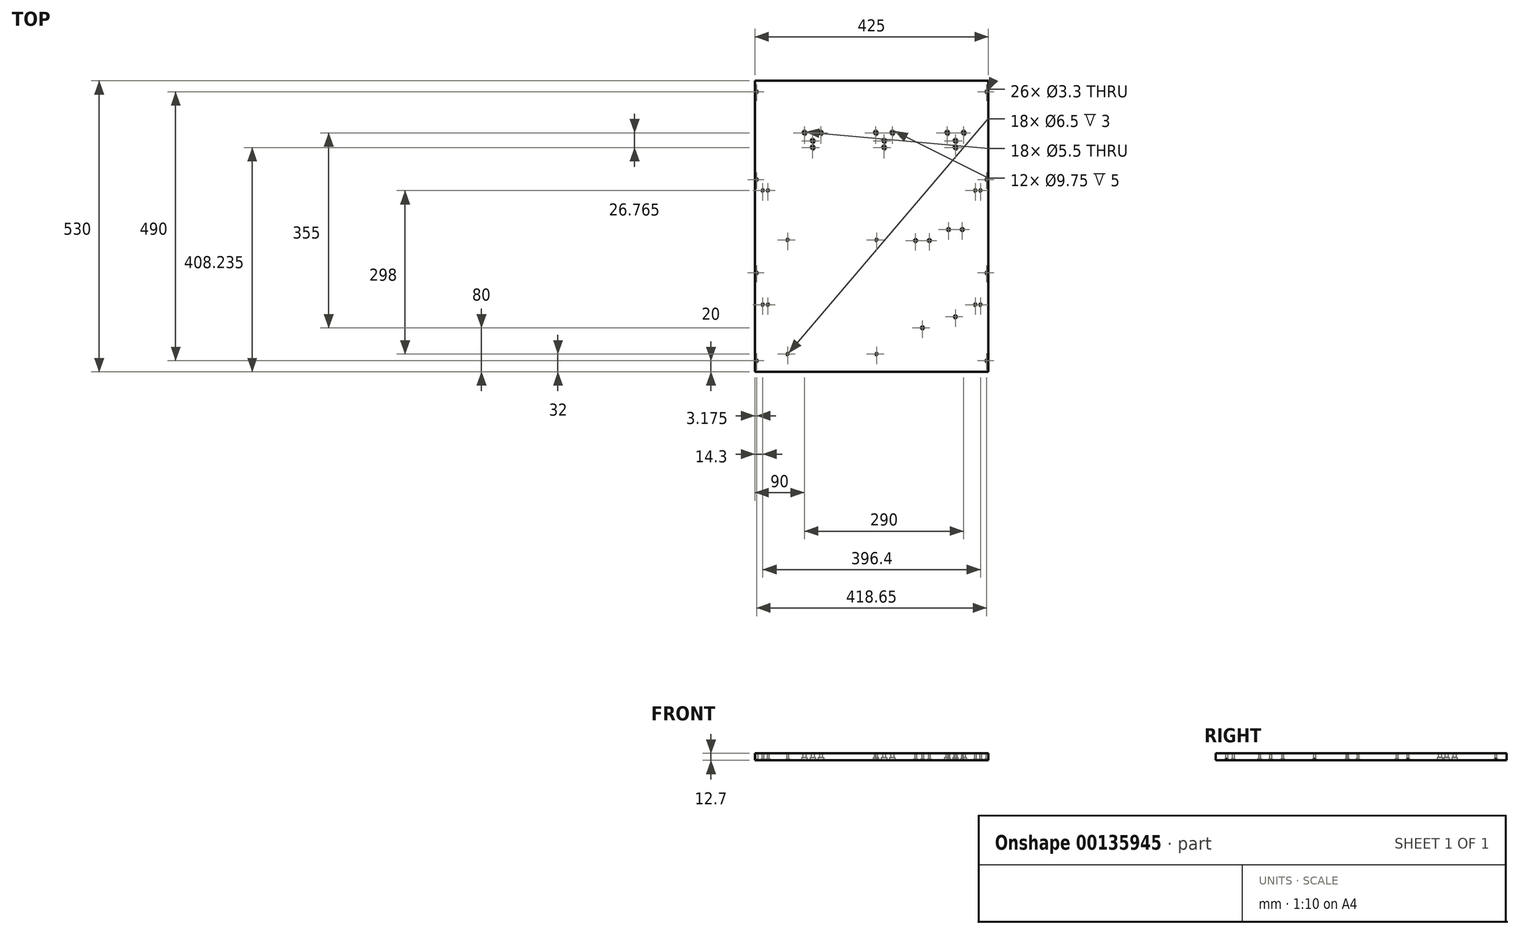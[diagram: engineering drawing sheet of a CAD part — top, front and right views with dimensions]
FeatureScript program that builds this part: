
annotation { "Feature Type Name" : "Feature", "Feature Type Description" : "" }
export const myFeature = defineFeature(function(context is Context, id is Id, definition is map)
    precondition{}
    {
        {
            var Q0;
            Q0=qCreatedBy(makeId("Top.planeOp"),FACE);
            var sketch = newSketch(context, id + "F0", { "sketchPlane" : qUnion([Q0])});
            skLineSegment(sketch, "E0.bottom", {"start": v(212.5, -265) * mm, "end": v(-212.5, -265) * mm});
            skLineSegment(sketch, "E0.top", {"start": v(212.5, 265) * mm, "end": v(-212.5, 265) * mm});
            skLineSegment(sketch, "E0.left", {"start": v(212.5, -265) * mm, "end": v(212.5, 265) * mm});
            skLineSegment(sketch, "E0.right", {"start": v(-212.5, -265) * mm, "end": v(-212.5, 265) * mm});
            skPoint(sketch, "E0.middle", {"position": v(0, 0) * mm});
            skLineSegment(sketch, "E1.top", {"start": v(81.24, -196.03) * mm, "end": v(129.3, -196.03) * mm});
            skSolve(sketch);
        }
        {
            var Q0;
            Q0 = qSketchRegion(id + "F0", true);
            extrude(context, id + "F1", {"entities" : qUnion([Q0]), "endBound" : BoundingType.SYMMETRIC, "depth" : 12.7 * mm});
        }
        {
            var Q0;
            Q0=makeQuery(id+"F1.opExtrude","CAP_FACE",FACE,{"disambiguationData":[OSD([sQuery(id+"F0.wireOp",EDGE,"E0.bottom"),sQuery(id+"F0.wireOp",EDGE,"E0.top"),sQuery(id+"F0.wireOp",EDGE,"E0.left"),sQuery(id+"F0.wireOp",EDGE,"E0.right")])],"isStart":true});
            var sketch = newSketch(context, id + "F2", { "sketchPlane" : qUnion([Q0])});
            skCircle(sketch, "E2", {"center": v(-209.33, 245) * mm, "radius": 2 * mm});
            skCircle(sketch, "E3", {"center": v(-209.33, 85) * mm, "radius": 2 * mm});
            skCircle(sketch, "E4.MirrorC", {"center": v(-209.33, -85) * mm, "radius": 2 * mm});
            skCircle(sketch, "E5.MirrorC", {"center": v(-209.33, -245) * mm, "radius": 2 * mm});
            skCircle(sketch, "E6.MirrorC", {"center": v(209.33, 245) * mm, "radius": 2 * mm});
            skCircle(sketch, "E7.MirrorC", {"center": v(209.33, 85) * mm, "radius": 2 * mm});
            skCircle(sketch, "E8.MirrorC", {"center": v(209.33, -85) * mm, "radius": 2 * mm});
            skCircle(sketch, "E9.MirrorC", {"center": v(209.33, -245) * mm, "radius": 2 * mm});
            skCircle(sketch, "E10", {"center": v(-198.2, 143) * mm, "radius": 2 * mm});
            skLineSegment(sketch, "E11", {"start": v(0, 0) * mm, "end": v(0, 264.7) * mm});
            skCircle(sketch, "E12", {"center": v(-188.7, 143) * mm, "radius": 2 * mm});
            skCircle(sketch, "E13.MirrorC", {"center": v(198.2, 143) * mm, "radius": 2 * mm});
            skCircle(sketch, "E14.MirrorC", {"center": v(188.7, 143) * mm, "radius": 2 * mm});
            skCircle(sketch, "E15", {"center": v(-198.2, -65) * mm, "radius": 2 * mm});
            skCircle(sketch, "E16", {"center": v(-188.7, -65) * mm, "radius": 2 * mm});
            skCircle(sketch, "E17.MirrorC", {"center": v(188.7, -65) * mm, "radius": 2 * mm});
            skCircle(sketch, "E18.MirrorC", {"center": v(198.2, -65) * mm, "radius": 2 * mm});
            skSolve(sketch);
        }
        {
            var Q0;
            Q0=sQuery(id+"F2.wireOp",VERTEX,"E2.center");
            var Q1;
            Q1=sQuery(id+"F2.wireOp",VERTEX,"E3.center");
            var Q2;
            Q2=sQuery(id+"F2.wireOp",VERTEX,"E4.MirrorC.center");
            var Q3;
            Q3=sQuery(id+"F2.wireOp",VERTEX,"E5.MirrorC.center");
            var Q4;
            Q4=sQuery(id+"F2.wireOp",VERTEX,"E9.MirrorC.center");
            var Q5;
            Q5=sQuery(id+"F2.wireOp",VERTEX,"E8.MirrorC.center");
            var Q6;
            Q6=sQuery(id+"F2.wireOp",VERTEX,"E7.MirrorC.center");
            var Q7;
            Q7=sQuery(id+"F2.wireOp",VERTEX,"E6.MirrorC.center");
            var Q8;
            Q8=sQuery(id+"F2.wireOp",VERTEX,"E10.center");
            var Q9;
            Q9=sQuery(id+"F2.wireOp",VERTEX,"WoDvKdXF-PdJz-WFzz-Z4uX-elENKUMFdGKx.center");
            var Q10;
            Q10=sQuery(id+"F2.wireOp",VERTEX,"axoy2mSQ-Yy3T-ROeZ-40XW-cdWlI4RzoubP.center");
            var Q11;
            Q11=sQuery(id+"F2.wireOp",VERTEX,"Gf7lKQ4c-8bLx-3h7W-wmy7-qyMdfDCTACcy.center");
            var Q12;
            Q12=sQuery(id+"F2.wireOp",VERTEX,"afeb9733-eb6e-4099-b4cc-138f5442d24a0.MirrorC.center");
            var Q13;
            Q13=sQuery(id+"F2.wireOp",VERTEX,"5a1a8710-edd7-43ff-9459-da1546c242ab0.MirrorC.center");
            var Q14;
            Q14=sQuery(id+"F2.wireOp",VERTEX,"c1e0f906-5fed-4c0f-b8fc-75f51ee2fa860.MirrorC.center");
            var Q15;
            Q15=sQuery(id+"F2.wireOp",VERTEX,"86eb54a1-4769-462b-b598-50202e1166000.MirrorC.center");
            var Q16;
            Q16=sQuery(id+"F2.wireOp",VERTEX,"6J1cC2zl-gnNa-lyWi-kusl-kWZGhb2Tm6Yi.center");
            var Q17;
            Q17=sQuery(id+"F2.wireOp",VERTEX,"2Pyidt3F-xQNL-qOz5-DrPg-jibaZAFIGgOY.center");
            var Q18;
            Q18=sQuery(id+"F2.wireOp",VERTEX,"3b745f28-dec8-4eaf-b7a0-753a52fb6e040.MirrorC.center");
            var Q19;
            Q19=sQuery(id+"F2.wireOp",VERTEX,"65bc9fd0-061f-4973-9c23-7b2eaf92318f0.MirrorC.center");
            var Q20;
            Q20=sQuery(id+"F2.wireOp",VERTEX,"E12.center");
            var Q21;
            Q21=sQuery(id+"F2.wireOp",VERTEX,"E13.MirrorC.center");
            var Q22;
            Q22=sQuery(id+"F2.wireOp",VERTEX,"E14.MirrorC.center");
            var Q23;
            Q23=sQuery(id+"F2.wireOp",VERTEX,"E15.center");
            var Q24;
            Q24=sQuery(id+"F2.wireOp",VERTEX,"E16.center");
            var Q25;
            Q25=sQuery(id+"F2.wireOp",VERTEX,"E17.MirrorC.center");
            var Q26;
            Q26=sQuery(id+"F2.wireOp",VERTEX,"E18.MirrorC.center");
            var Q27;
            Q27=makeQuery(id+"F1.opExtrude","SWEPT_BODY",BODY,{"disambiguationData":[OSD([sQuery(id+"F0.wireOp",EDGE,"E0.bottom"),sQuery(id+"F0.wireOp",EDGE,"E0.top"),sQuery(id+"F0.wireOp",EDGE,"E0.left"),sQuery(id+"F0.wireOp",EDGE,"E0.right")])]});
            hole(context, id + "F3", {"style" : HoleStyle.C_BORE, "endStyle" : HoleEndStyle.THROUGH, "standardTappedOrClearance" : lookupTablePath({ "standard" : "ISO", "fit" : "Normal", "size" : "M3", "type" : "Clearance" }), "standardBlindInLast" : lookupTablePath({ "fit" : "Standard", "standard" : "ISO", "size" : "M3", "type" : "Clearance" }), "holeDiameter" : 3.3 * mm, "cBoreDiameter" : 6.5 * mm, "cBoreDepth" : 3 * mm, "locations" : qUnion([Q0, Q1, Q2, Q3, Q4, Q5, Q6, Q7, Q8, Q9, Q10, Q11, Q12, Q13, Q14, Q15, Q16, Q17, Q18, Q19, Q20, Q21, Q22, Q23, Q24, Q25, Q26]), "scope" : qUnion([Q27]), "isTappedThrough" : true});
        }
        {
            var Q0;
            Q0=makeQuery(id+"F1.opExtrude","CAP_FACE",FACE,{"disambiguationData":[OSD([sQuery(id+"F0.wireOp",EDGE,"E0.bottom"),sQuery(id+"F0.wireOp",EDGE,"E0.top"),sQuery(id+"F0.wireOp",EDGE,"E0.left"),sQuery(id+"F0.wireOp",EDGE,"E0.right")])],"isStart":true});
            var sketch = newSketch(context, id + "F4", { "sketchPlane" : qUnion([Q0])});
            skCircle(sketch, "E19", {"center": v(-122.5, -170) * mm, "radius": 2 * mm});
            skCircle(sketch, "E20", {"center": v(-92.5, -170) * mm, "radius": 2 * mm});
            skCircle(sketch, "E21", {"center": v(-107.5, -155.23) * mm, "radius": 2 * mm});
            skCircle(sketch, "E22", {"center": v(-107.5, -143.23) * mm, "radius": 2 * mm});
            skCircle(sketch, "E23", {"center": v(137.5, -170) * mm, "radius": 2 * mm});
            skCircle(sketch, "E24", {"center": v(167.5, -170) * mm, "radius": 2 * mm});
            skCircle(sketch, "E25", {"center": v(152.5, -155.24) * mm, "radius": 2 * mm});
            skCircle(sketch, "E26", {"center": v(152.5, -143.24) * mm, "radius": 2 * mm});
            skCircle(sketch, "E27", {"center": v(7.5, -170) * mm, "radius": 2 * mm});
            skCircle(sketch, "E28", {"center": v(37.5, -170) * mm, "radius": 2 * mm});
            skCircle(sketch, "E29", {"center": v(22.5, -155.23) * mm, "radius": 2 * mm});
            skCircle(sketch, "E30", {"center": v(22.5, -143.23) * mm, "radius": 2 * mm});
            skSolve(sketch);
        }
        {
            var Q0;
            Q0=sQuery(id+"F4.wireOp",VERTEX,"E19.center");
            var Q1;
            Q1=sQuery(id+"F4.wireOp",VERTEX,"E20.center");
            var Q2;
            Q2=sQuery(id+"F4.wireOp",VERTEX,"E21.center");
            var Q3;
            Q3=sQuery(id+"F4.wireOp",VERTEX,"E22.center");
            var Q4;
            Q4=sQuery(id+"F4.wireOp",VERTEX,"E24.center");
            var Q5;
            Q5=sQuery(id+"F4.wireOp",VERTEX,"E25.center");
            var Q6;
            Q6=sQuery(id+"F4.wireOp",VERTEX,"E26.center");
            var Q7;
            Q7=sQuery(id+"F4.wireOp",VERTEX,"E23.center");
            var Q8;
            Q8=sQuery(id+"F4.wireOp",VERTEX,"E28.center");
            var Q9;
            Q9=sQuery(id+"F4.wireOp",VERTEX,"E27.center");
            var Q10;
            Q10=sQuery(id+"F4.wireOp",VERTEX,"E29.center");
            var Q11;
            Q11=sQuery(id+"F4.wireOp",VERTEX,"E30.center");
            var Q12;
            Q12=makeQuery(id+"F1.opExtrude","SWEPT_BODY",BODY,{"disambiguationData":[OSD([sQuery(id+"F0.wireOp",EDGE,"E0.bottom"),sQuery(id+"F0.wireOp",EDGE,"E0.top"),sQuery(id+"F0.wireOp",EDGE,"E0.left"),sQuery(id+"F0.wireOp",EDGE,"E0.right")])]});
            hole(context, id + "F5", {"style" : HoleStyle.C_BORE, "endStyle" : HoleEndStyle.THROUGH, "standardTappedOrClearance" : lookupTablePath({ "standard" : "ISO", "fit" : "Normal", "size" : "M5", "type" : "Clearance" }), "standardBlindInLast" : lookupTablePath({ "fit" : "Standard", "standard" : "ISO", "size" : "M5", "type" : "Clearance" }), "holeDiameter" : 5.5 * mm, "cBoreDiameter" : 9.75 * mm, "cBoreDepth" : 5 * mm, "locations" : qUnion([Q0, Q1, Q2, Q3, Q4, Q5, Q6, Q7, Q8, Q9, Q10, Q11]), "scope" : qUnion([Q12]), "isTappedThrough" : true});
        }
        {
            var Q0;
            Q0=makeQuery(id+"F1.opExtrude","CAP_FACE",FACE,{"disambiguationData":[OSD([sQuery(id+"F0.wireOp",EDGE,"E0.bottom"),sQuery(id+"F0.wireOp",EDGE,"E0.top"),sQuery(id+"F0.wireOp",EDGE,"E0.left"),sQuery(id+"F0.wireOp",EDGE,"E0.right")])],"isStart":true});
            var sketch = newSketch(context, id + "F6", { "sketchPlane" : qUnion([Q0])});
            skCircle(sketch, "E31", {"center": v(152.5, 165) * mm, "radius": 1.5 * mm});
            skCircle(sketch, "E32", {"center": v(165, 6) * mm, "radius": 1.5 * mm});
            skCircle(sketch, "E33", {"center": v(140, 6) * mm, "radius": 1.5 * mm});
            skCircle(sketch, "E34", {"center": v(92.5, 185) * mm, "radius": 1.5 * mm});
            skCircle(sketch, "E35", {"center": v(105, 26) * mm, "radius": 1.5 * mm});
            skCircle(sketch, "E36", {"center": v(80, 26) * mm, "radius": 1.5 * mm});
            skSolve(sketch);
        }
        {
            var Q0;
            Q0=sQuery(id+"F6.wireOp",VERTEX,"E31.center");
            var Q1;
            Q1=sQuery(id+"F6.wireOp",VERTEX,"E32.center");
            var Q2;
            Q2=sQuery(id+"F6.wireOp",VERTEX,"E33.center");
            var Q3;
            Q3=sQuery(id+"F6.wireOp",VERTEX,"E34.center");
            var Q4;
            Q4=sQuery(id+"F6.wireOp",VERTEX,"E35.center");
            var Q5;
            Q5=sQuery(id+"F6.wireOp",VERTEX,"E36.center");
            var Q6;
            Q6=makeQuery(id+"F1.opExtrude","SWEPT_BODY",BODY,{"disambiguationData":[OSD([sQuery(id+"F0.wireOp",EDGE,"E0.bottom"),sQuery(id+"F0.wireOp",EDGE,"E0.top"),sQuery(id+"F0.wireOp",EDGE,"E0.left"),sQuery(id+"F0.wireOp",EDGE,"E0.right")])]});
            hole(context, id + "F7", {"style" : HoleStyle.C_BORE, "endStyle" : HoleEndStyle.THROUGH, "standardTappedOrClearance" : lookupTablePath({ "standard" : "ISO", "fit" : "Normal", "size" : "M3", "type" : "Clearance" }), "standardBlindInLast" : lookupTablePath({ "fit" : "Standard", "standard" : "ISO", "size" : "M3", "type" : "Clearance" }), "holeDiameter" : 3.3 * mm, "cBoreDiameter" : 6.5 * mm, "cBoreDepth" : 3 * mm, "locations" : qUnion([Q0, Q1, Q2, Q3, Q4, Q5]), "scope" : qUnion([Q6]), "isTappedThrough" : true});
        }
        {
            var Q0;
            Q0=makeQuery(id+"F1.opExtrude","CAP_FACE",FACE,{"disambiguationData":[OSD([sQuery(id+"F0.wireOp",EDGE,"E0.bottom"),sQuery(id+"F0.wireOp",EDGE,"E0.top"),sQuery(id+"F0.wireOp",EDGE,"E0.left"),sQuery(id+"F0.wireOp",EDGE,"E0.right")])],"isStart":false});
            var sketch = newSketch(context, id + "F8", { "sketchPlane" : qUnion([Q0])});
            skCircle(sketch, "E37", {"center": v(80, -26) * mm, "radius": 3 * mm});
            skCircle(sketch, "E38", {"center": v(105, -26) * mm, "radius": 3 * mm});
            skCircle(sketch, "E39", {"center": v(140, -6) * mm, "radius": 3 * mm});
            skCircle(sketch, "E40", {"center": v(165, -6) * mm, "radius": 3 * mm});
            skCircle(sketch, "E41", {"center": v(152.5, -165) * mm, "radius": 3 * mm});
            skCircle(sketch, "E42", {"center": v(92.5, -185) * mm, "radius": 3 * mm});
            skSolve(sketch);
        }
        {
            var Q0;
            Q0=sQuery(id+"F8.wireOp",VERTEX,"E40.center");
            var Q1;
            Q1=sQuery(id+"F8.wireOp",VERTEX,"E39.center");
            var Q2;
            Q2=sQuery(id+"F8.wireOp",VERTEX,"E38.center");
            var Q3;
            Q3=sQuery(id+"F8.wireOp",VERTEX,"E38.center");
            var Q4;
            Q4=sQuery(id+"F8.wireOp",VERTEX,"E37.center");
            var Q5;
            Q5=sQuery(id+"F8.wireOp",VERTEX,"E41.center");
            var Q6;
            Q6=sQuery(id+"F8.wireOp",VERTEX,"E42.center");
            var Q7;
            Q7=makeQuery(id+"F1.opExtrude","SWEPT_BODY",BODY,{"disambiguationData":[OSD([sQuery(id+"F0.wireOp",EDGE,"E0.bottom"),sQuery(id+"F0.wireOp",EDGE,"E0.top"),sQuery(id+"F0.wireOp",EDGE,"E0.left"),sQuery(id+"F0.wireOp",EDGE,"E0.right")])]});
            hole(context, id + "F9", {"style" : HoleStyle.SIMPLE, "endStyle" : HoleEndStyle.BLIND, "standardTappedOrClearance" : lookupTablePath({ "standard" : "ISO", "fit" : "Normal", "size" : "M5", "type" : "Clearance" }), "standardBlindInLast" : lookupTablePath({ "fit" : "Standard", "standard" : "ISO", "size" : "M5", "type" : "Clearance" }), "holeDiameter" : 5.5 * mm, "holeDepth" : 1 * mm, "startFromSketch" : true, "locations" : qUnion([Q0, Q1, Q2, Q3, Q4, Q5, Q6]), "scope" : qUnion([Q7])});
        }
        {
            var Q0;
            Q0=makeQuery(id+"F1.opExtrude","CAP_FACE",FACE,{"disambiguationData":[OSD([sQuery(id+"F0.wireOp",EDGE,"E0.bottom"),sQuery(id+"F0.wireOp",EDGE,"E0.top"),sQuery(id+"F0.wireOp",EDGE,"E0.left"),sQuery(id+"F0.wireOp",EDGE,"E0.right")])],"isStart":true});
            var sketch = newSketch(context, id + "F10", { "sketchPlane" : qUnion([Q0])});
            skCircle(sketch, "E43", {"center": v(-153, 233) * mm, "radius": 2 * mm});
            skCircle(sketch, "E44", {"center": v(9, 233) * mm, "radius": 2 * mm});
            skCircle(sketch, "E45", {"center": v(-153, 25) * mm, "radius": 2 * mm});
            skCircle(sketch, "E46", {"center": v(9, 25) * mm, "radius": 2 * mm});
            skSolve(sketch);
        }
        {
            var Q0;
            Q0=sQuery(id+"F10.wireOp",VERTEX,"E43.center");
            var Q1;
            Q1=sQuery(id+"F10.wireOp",VERTEX,"E44.center");
            var Q2;
            Q2=sQuery(id+"F10.wireOp",VERTEX,"E46.center");
            var Q3;
            Q3=sQuery(id+"F10.wireOp",VERTEX,"E45.center");
            var Q4;
            Q4=makeQuery(id+"F1.opExtrude","SWEPT_BODY",BODY,{"disambiguationData":[OSD([sQuery(id+"F0.wireOp",EDGE,"E0.bottom"),sQuery(id+"F0.wireOp",EDGE,"E0.top"),sQuery(id+"F0.wireOp",EDGE,"E0.left"),sQuery(id+"F0.wireOp",EDGE,"E0.right")])]});
            hole(context, id + "F11", {"style" : HoleStyle.C_BORE, "endStyle" : HoleEndStyle.THROUGH, "standardTappedOrClearance" : lookupTablePath({ "standard" : "ISO", "fit" : "Normal", "size" : "M3", "type" : "Clearance" }), "standardBlindInLast" : lookupTablePath({ "fit" : "Standard", "standard" : "ISO", "size" : "M3", "type" : "Clearance" }), "holeDiameter" : 3.3 * mm, "cBoreDiameter" : 6.5 * mm, "cBoreDepth" : 3 * mm, "startFromSketch" : true, "locations" : qUnion([Q0, Q1, Q2, Q3]), "scope" : qUnion([Q4]), "isTappedThrough" : true});
        }
    });
